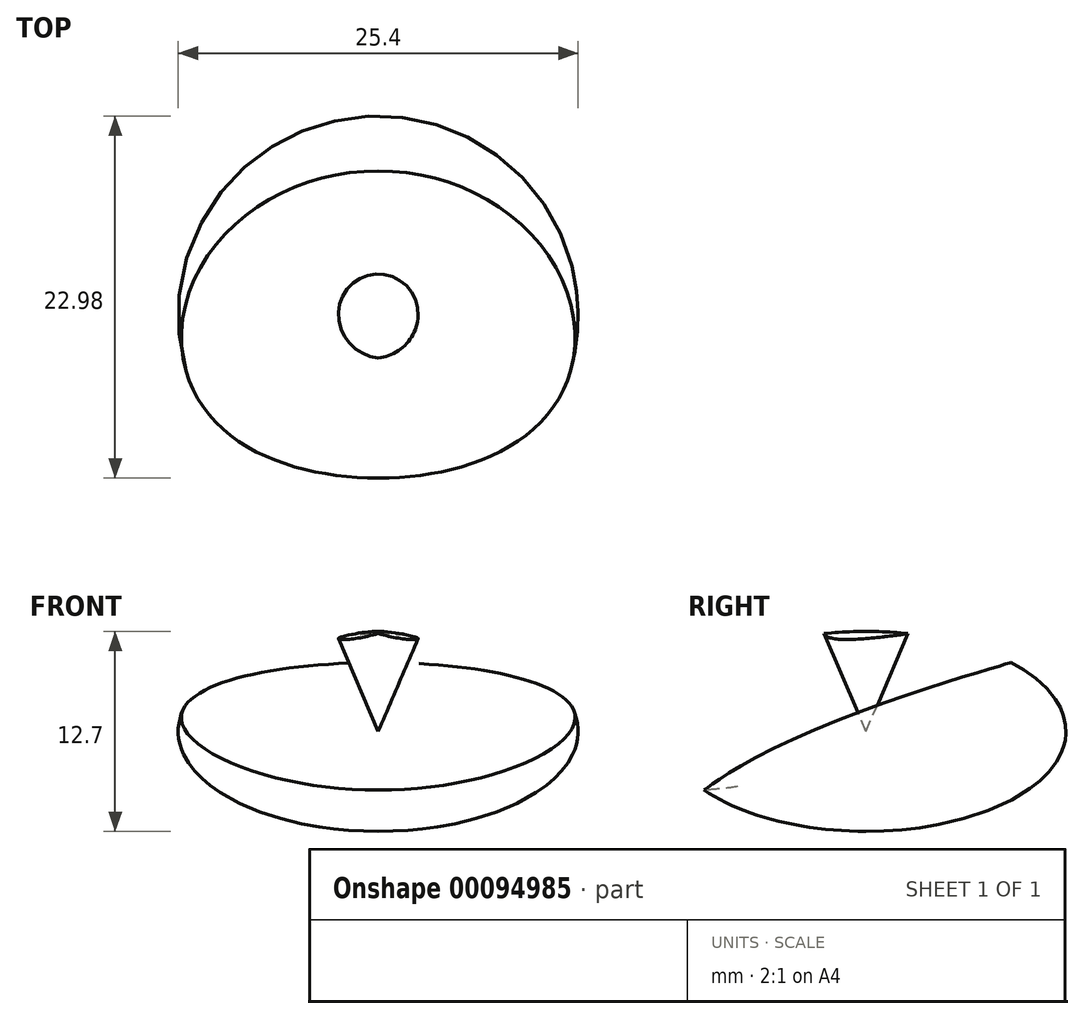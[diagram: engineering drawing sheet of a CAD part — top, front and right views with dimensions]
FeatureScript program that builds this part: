
annotation { "Feature Type Name" : "Feature", "Feature Type Description" : "" }
export const myFeature = defineFeature(function(context is Context, id is Id, definition is map)
    precondition{}
    {
        {
            var Q0;
            Q0=qCreatedBy(makeId("Right.planeOp"),FACE);
            var sketch = newSketch(context, id + "F0", { "sketchPlane" : qUnion([Q0])});
            skEllipse(sketch, "E0", {"center": v(32.9, -34.8) * mm, "majorRadius": 12.7 * mm, "minorRadius": 6.35 * mm, "majorAxis": v(1, 0)});
            skArc(sketch, "E1", {"start": v(41.65, -30.82) * mm, "mid": v(44.26, -5.42) * mm, "end": v(18.92, -2.29) * mm});
            skLineSegment(sketch, "E2", {"start": v(18.92, -2.29) * mm, "end": v(32.9, -34.8) * mm});
            skFitSpline(sketch, "E3", {"points": [v(40.84, -29.85) * mm, v(41.5, -39.46) * mm, v(-36.9, -98.21) * mm], "startDerivative": vector(25.92, -31.17) * mm, "endDerivative": vector(-0.88, 16.62) * mm, "construction": true});
            skLineSegment(sketch, "E4", {"start": v(32.9, -28.45) * mm, "end": v(32.9, -41.15) * mm});
            skLineSegment(sketch, "E5", {"start": v(32.9, -41.15) * mm, "end": v(32.9, -40.64) * mm});
            skLineSegment(sketch, "E6", {"start": v(32.9, -40.64) * mm, "end": v(36.87, -40.64) * mm, "construction": true});
            skLineSegment(sketch, "E7", {"start": v(38.84, -40.33) * mm, "end": v(40.64, -39.74) * mm, "construction": true});
            skPoint(sketch, "E8.visualSharp", {"position": v(37.88, -40.64) * mm});
            skArc(sketch, "E8.filletArc", {"start": v(36.87, -40.64) * mm, "mid": v(37.87, -40.56) * mm, "end": v(38.84, -40.33) * mm, "construction": true});
            skArc(sketch, "E9.filletArc", {"start": v(40.64, -39.74) * mm, "mid": v(41.44, -39.31) * mm, "end": v(42.03, -38.63) * mm, "construction": true});
            skFitSpline(sketch, "E10", {"points": [v(40.84, -29.85) * mm, v(42.03, -38.63) * mm, v(40.64, -39.74) * mm, v(38.84, -40.33) * mm, v(36.87, -40.64) * mm, v(32.9, -40.64) * mm], "startDerivative": vector(37.49, -37.26) * mm, "endDerivative": vector(-19.78, 0.48) * mm});
            skSolve(sketch);
        }
        {
            var Q0;
            {var subQ3=sQuery(id+"F0.wireOp",EDGE,"E0");var subQ7=makeQuery(id+"F0.imprint","INTERSECT",VERTEX,{"disambiguationData":[OD(0.0)],"derivedFrom":[subQ3,sQuery(id+"F0.wireOp",EDGE,"E3")]});Q0=makeQuery(id+"F0.imprint","IMPRINT",FACE,{"disambiguationData":[TD([[makeQuery(id+"F0.imprint","IMPRINT",EDGE,{"disambiguationData":[TD([[subQ7,1.0]])],"derivedFrom":subQ3}),-1.0]])]});}
            var Q1;
            Q1=sQuery(id+"F0.wireOp",EDGE,"E2");
            revolve(context, id + "F1", {"entities" : qUnion([Q0]), "axis" : qUnion([Q1]), "revolveType" : RevolveType.FULL});
        }
        {
            var Q0;
            {var subQ1=sQuery(id+"F0.wireOp",EDGE,"E0");var subQ4=sQuery(id+"F0.wireOp",EDGE,"E4");var subQ7=makeQuery(id+"F0.imprint","INTERSECT",VERTEX,{"derivedFrom":[subQ1,subQ4]});Q0=makeQuery(id+"F0.imprint","IMPRINT",FACE,{"disambiguationData":[TD([[makeQuery(id+"F0.imprint","IMPRINT",EDGE,{"disambiguationData":[TD([[subQ7,1.0]])],"derivedFrom":subQ1}),1.0]])]});}
            var Q1;
            Q1=sQuery(id+"F0.wireOp",EDGE,"E4");
            revolve(context, id + "F2", {"operationType" : NewBodyOperationType.ADD, "entities" : qUnion([Q0]), "axis" : qUnion([Q1]), "revolveType" : RevolveType.FULL});
        }
    });
